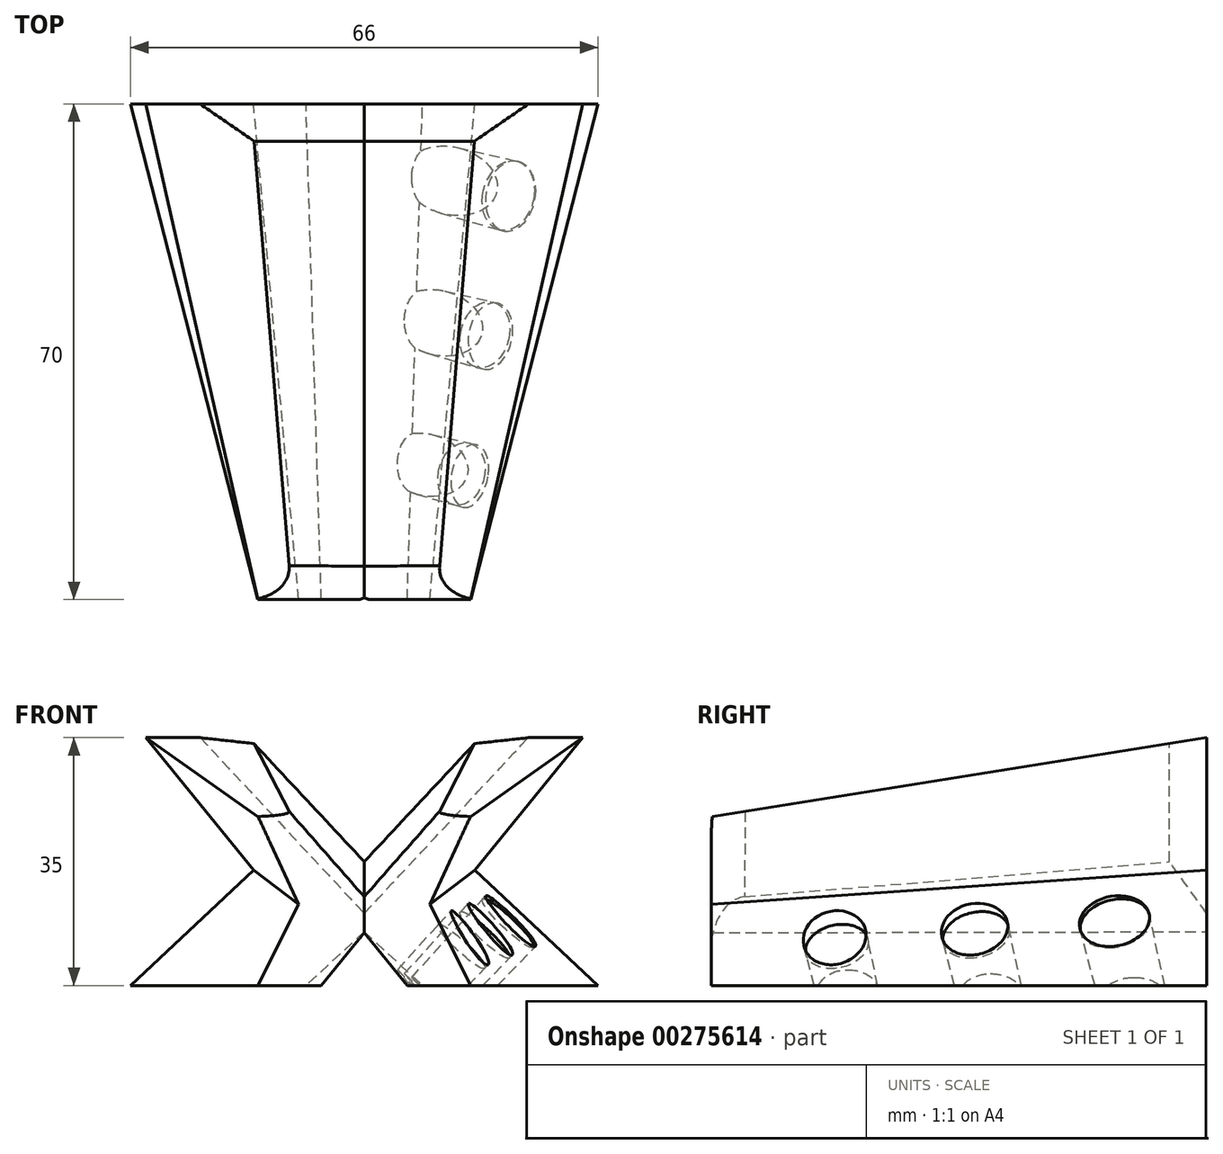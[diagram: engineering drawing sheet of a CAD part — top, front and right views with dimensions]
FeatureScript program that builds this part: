
annotation { "Feature Type Name" : "Feature", "Feature Type Description" : "" }
export const myFeature = defineFeature(function(context is Context, id is Id, definition is map)
    precondition{}
    {
        {
            var Q0;
            Q0=qCreatedBy(makeId("Front.planeOp"),FACE);
            var sketch = newSketch(context, id + "F0", { "sketchPlane" : qUnion([Q0])});
            skLineSegment(sketch, "E0.bottom", {"start": v(-15, 24) * mm, "end": v(15, 24) * mm, "construction": true});
            skLineSegment(sketch, "E0.top", {"start": v(-15, 0) * mm, "end": v(15, 0) * mm, "construction": true});
            skLineSegment(sketch, "E0.left", {"start": v(-15, 24) * mm, "end": v(-15, 0) * mm, "construction": true});
            skLineSegment(sketch, "E0.right", {"start": v(15, 24) * mm, "end": v(15, 0) * mm, "construction": true});
            skLineSegment(sketch, "E1", {"start": v(0, 0) * mm, "end": v(0, 24) * mm, "construction": true});
            skLineSegment(sketch, "E2", {"start": v(-15, 24) * mm, "end": v(-10.26, 24) * mm});
            skLineSegment(sketch, "E3", {"start": v(0, 12) * mm, "end": v(-10.26, 24) * mm});
            skLineSegment(sketch, "E4", {"start": v(-15, 24) * mm, "end": v(-15, 18.21) * mm});
            skLineSegment(sketch, "E5", {"start": v(-9.17, 11.4) * mm, "end": v(-15, 18.21) * mm});
            skLineSegment(sketch, "E6", {"start": v(-15, 6.41) * mm, "end": v(-9.17, 11.4) * mm});
            skLineSegment(sketch, "E7", {"start": v(-15, 6.41) * mm, "end": v(-15, 0) * mm});
            skLineSegment(sketch, "E8", {"start": v(-7.14, 0) * mm, "end": v(0, 6.41) * mm});
            skLineSegment(sketch, "E9", {"start": v(-15, 0) * mm, "end": v(-7.14, 0) * mm});
            skLineSegment(sketch, "E10.MirrorCS", {"start": v(0, 12) * mm, "end": v(10.26, 24) * mm});
            skLineSegment(sketch, "E11.MirrorCS", {"start": v(15, 24) * mm, "end": v(10.26, 24) * mm});
            skLineSegment(sketch, "E12.MirrorCS", {"start": v(15, 24) * mm, "end": v(15, 18.21) * mm});
            skLineSegment(sketch, "E13.MirrorCS", {"start": v(9.17, 11.4) * mm, "end": v(15, 18.21) * mm});
            skLineSegment(sketch, "E14.MirrorCS", {"start": v(15, 6.41) * mm, "end": v(9.17, 11.4) * mm});
            skLineSegment(sketch, "E15.MirrorCS", {"start": v(15, 6.41) * mm, "end": v(15, 0) * mm});
            skLineSegment(sketch, "E16.MirrorCS", {"start": v(15, 0) * mm, "end": v(7.14, 0) * mm});
            skLineSegment(sketch, "E17.MirrorCS", {"start": v(7.14, 0) * mm, "end": v(0, 6.41) * mm});
            skSolve(sketch);
        }
        {
            var Q0;
            Q0=qCreatedBy(makeId("Front.planeOp"),FACE);
            cPlane(context, id + "F1", {"entities" : qUnion([Q0]), "cplaneType" : CPlaneType.OFFSET, "offset" : 70 * mm, "oppositeDirection" : true, "width" : 150 * mm, "height" : 150 * mm});
        }
        {
            var Q0;
            Q0=qCreatedBy(id+"F1.planeOp",FACE);
            var sketch = newSketch(context, id + "F2", { "sketchPlane" : qUnion([Q0])});
            skLineSegment(sketch, "E18", {"start": v(0, 7.6) * mm, "end": v(-8.22, 0) * mm});
            skLineSegment(sketch, "E19", {"start": v(-8.22, 0) * mm, "end": v(-33, 0) * mm});
            skLineSegment(sketch, "E20", {"start": v(-33, 0) * mm, "end": v(-15.64, 16.3) * mm});
            skLineSegment(sketch, "E21", {"start": v(-15.64, 16.3) * mm, "end": v(-30.87, 35) * mm});
            skLineSegment(sketch, "E22", {"start": v(-30.87, 35) * mm, "end": v(-16, 35) * mm});
            skLineSegment(sketch, "E23", {"start": v(-16, 35) * mm, "end": v(0, 17.93) * mm});
            skLineSegment(sketch, "E24.MirrorCS", {"start": v(16, 35) * mm, "end": v(0, 17.93) * mm});
            skLineSegment(sketch, "E25.MirrorCS", {"start": v(30.87, 35) * mm, "end": v(16, 35) * mm});
            skLineSegment(sketch, "E26.MirrorCS", {"start": v(15.64, 16.3) * mm, "end": v(30.87, 35) * mm});
            skLineSegment(sketch, "E27.MirrorCS", {"start": v(33, 0) * mm, "end": v(15.64, 16.3) * mm});
            skLineSegment(sketch, "E28.MirrorCS", {"start": v(8.22, 0) * mm, "end": v(33, 0) * mm});
            skLineSegment(sketch, "E29.MirrorCS", {"start": v(0, 7.6) * mm, "end": v(8.22, 0) * mm});
            skSolve(sketch);
        }
        {
            var Q0;
            Q0=qCreatedBy(makeId("Front.planeOp"),FACE);
            var sketch = newSketch(context, id + "F3", { "sketchPlane" : qUnion([Q0])});
            skLineSegment(sketch, "E30", {"start": v(0, 12.13) * mm, "end": v(10.24, 23.85) * mm});
            skLineSegment(sketch, "E31", {"start": v(10.24, 23.85) * mm, "end": v(14.99, 23.85) * mm});
            skLineSegment(sketch, "E32", {"start": v(14.99, 23.85) * mm, "end": v(9.27, 11.44) * mm});
            skLineSegment(sketch, "E33", {"start": v(9.27, 11.44) * mm, "end": v(15.04, 0) * mm});
            skLineSegment(sketch, "E34", {"start": v(15.04, 0) * mm, "end": v(6.07, 0) * mm});
            skLineSegment(sketch, "E35", {"start": v(6.07, 0) * mm, "end": v(0, 7.44) * mm});
            skLineSegment(sketch, "E36.MirrorCS", {"start": v(0, 12.13) * mm, "end": v(-10.24, 23.85) * mm});
            skLineSegment(sketch, "E37.MirrorCS", {"start": v(-10.24, 23.85) * mm, "end": v(-14.99, 23.85) * mm});
            skLineSegment(sketch, "E38.MirrorCS", {"start": v(-14.99, 23.85) * mm, "end": v(-9.27, 11.44) * mm});
            skLineSegment(sketch, "E39.MirrorCS", {"start": v(-9.27, 11.44) * mm, "end": v(-15.04, 0) * mm});
            skLineSegment(sketch, "E40.MirrorCS", {"start": v(-6.07, 0) * mm, "end": v(0, 7.44) * mm});
            skLineSegment(sketch, "E41.MirrorCS", {"start": v(-15.04, 0) * mm, "end": v(-6.07, 0) * mm});
            skSolve(sketch);
        }
        {
            var Q0;
            Q0=makeQuery(id+"F3.imprint","IMPRINT",FACE,{"disambiguationData":[TD([[makeQuery(id+"F3.imprint","IMPRINT",EDGE,{"derivedFrom":sQuery(id+"F3.wireOp",EDGE,"E30")}),-1.0]])]});
            var Q1;
            Q1=makeQuery(id+"F2.imprint","IMPRINT",FACE,{"disambiguationData":[TD([[makeQuery(id+"F2.imprint","IMPRINT",EDGE,{"derivedFrom":sQuery(id+"F2.wireOp",EDGE,"E18")}),-1.0]])]});
            loft(context, id + "F4", {"sheetProfilesArray" : [{ "sheetProfileEntities" : qUnion([Q0]) }, { "sheetProfileEntities" : qUnion([Q1]) }]});
        }
        {
            var Q0;
            Q0=makeQuery(id+"F4.opLoft","MID_CAP_VERTEX",VERTEX,{"disambiguationData":[OSD([sQuery(id+"F3.wireOp",EDGE,"E33"),sQuery(id+"F3.wireOp",EDGE,"E34")])],"capPos":0.0});
            var Q1;
            Q1=makeQuery(id+"F4.opLoft","MID_CAP_VERTEX",VERTEX,{"disambiguationData":[OSD([sQuery(id+"F2.wireOp",EDGE,"E26.MirrorCS"),sQuery(id+"F2.wireOp",EDGE,"E27.MirrorCS")])],"capPos":1.0});
            var Q2;
            Q2=makeQuery(id+"F4.opLoft","MID_CAP_VERTEX",VERTEX,{"disambiguationData":[OSD([sQuery(id+"F2.wireOp",EDGE,"E27.MirrorCS"),sQuery(id+"F2.wireOp",EDGE,"E28.MirrorCS")])],"capPos":1.0});
            cPlane(context, id + "F5", {"entities" : qUnion([Q0, Q1, Q2]), "cplaneType" : CPlaneType.THREE_POINT, "offset" : 25 * mm, "width" : 150 * mm, "height" : 150 * mm});
        }
        {
            var Q0;
            Q0=qCreatedBy(id+"F5.planeOp",FACE);
            var sketch = newSketch(context, id + "F6", { "sketchPlane" : qUnion([Q0])});
            skCircle(sketch, "E42", {"center": v(9.33, 18.55) * mm, "radius": 4.5 * mm});
            skCircle(sketch, "E43", {"center": v(13.81, 38.04) * mm, "radius": 4.75 * mm});
            skCircle(sketch, "E44", {"center": v(18.3, 57.53) * mm, "radius": 5 * mm});
            skLineSegment(sketch, "E45", {"start": v(5.06, 0) * mm, "end": v(23.54, 80.33) * mm, "construction": true});
            skSolve(sketch);
        }
        {
            var Q0;
            Q0 = qSketchRegion(id + "F6", true);
            extrude(context, id + "F7", {"entities" : qUnion([Q0]), "operationType" : NewBodyOperationType.REMOVE, "oppositeDirection" : true, "depth" : 22.7 * mm, "hasDraft" : true, "draftAngle" : 1 * degree, "draftPullDirection" : true, "hasSecondDirection" : true, "secondDirectionOppositeDirection" : false, "secondDirectionDepth" : 23.6 * mm});
        }
        {
            var Q0;
            Q0=makeQuery(id+"F4.opLoft","MID_CAP_EDGE",EDGE,{"disambiguationData":[OSD([sQuery(id+"F3.wireOp",EDGE,"E30"),sQuery(id+"F3.wireOp",EDGE,"E36.MirrorCS"),sQuery(id+"F3.wireOp",EDGE,"E37.MirrorCS")])],"capPos":0.0});
            var Q1;
            Q1=makeQuery(id+"F4.opLoft","MID_CAP_EDGE",EDGE,{"disambiguationData":[OSD([sQuery(id+"F3.wireOp",EDGE,"E30"),sQuery(id+"F3.wireOp",EDGE,"E31"),sQuery(id+"F3.wireOp",EDGE,"E36.MirrorCS")])],"capPos":0.0});
            fillet(context, id + "F8", {"entities" : qUnion([Q0, Q1]), "radius" : 5 * mm, "tangentPropagation" : true, "allowEdgeOverflow" : false});
        }
        {
            var Q0;
            Q0=makeQuery(id+"F4.opLoft","MID_CAP_EDGE",EDGE,{"disambiguationData":[OSD([sQuery(id+"F2.wireOp",EDGE,"E23"),sQuery(id+"F2.wireOp",EDGE,"E24.MirrorCS"),sQuery(id+"F2.wireOp",EDGE,"E25.MirrorCS")])],"capPos":1.0});
            var Q1;
            Q1=makeQuery(id+"F4.opLoft","MID_CAP_EDGE",EDGE,{"disambiguationData":[OSD([sQuery(id+"F2.wireOp",EDGE,"E22"),sQuery(id+"F2.wireOp",EDGE,"E23"),sQuery(id+"F2.wireOp",EDGE,"E24.MirrorCS")])],"capPos":1.0});
            chamfer(context, id + "F9", {"entities" : qUnion([Q0, Q1]), "width" : 5 * mm, "tangentPropagation" : true});
        }
    });
